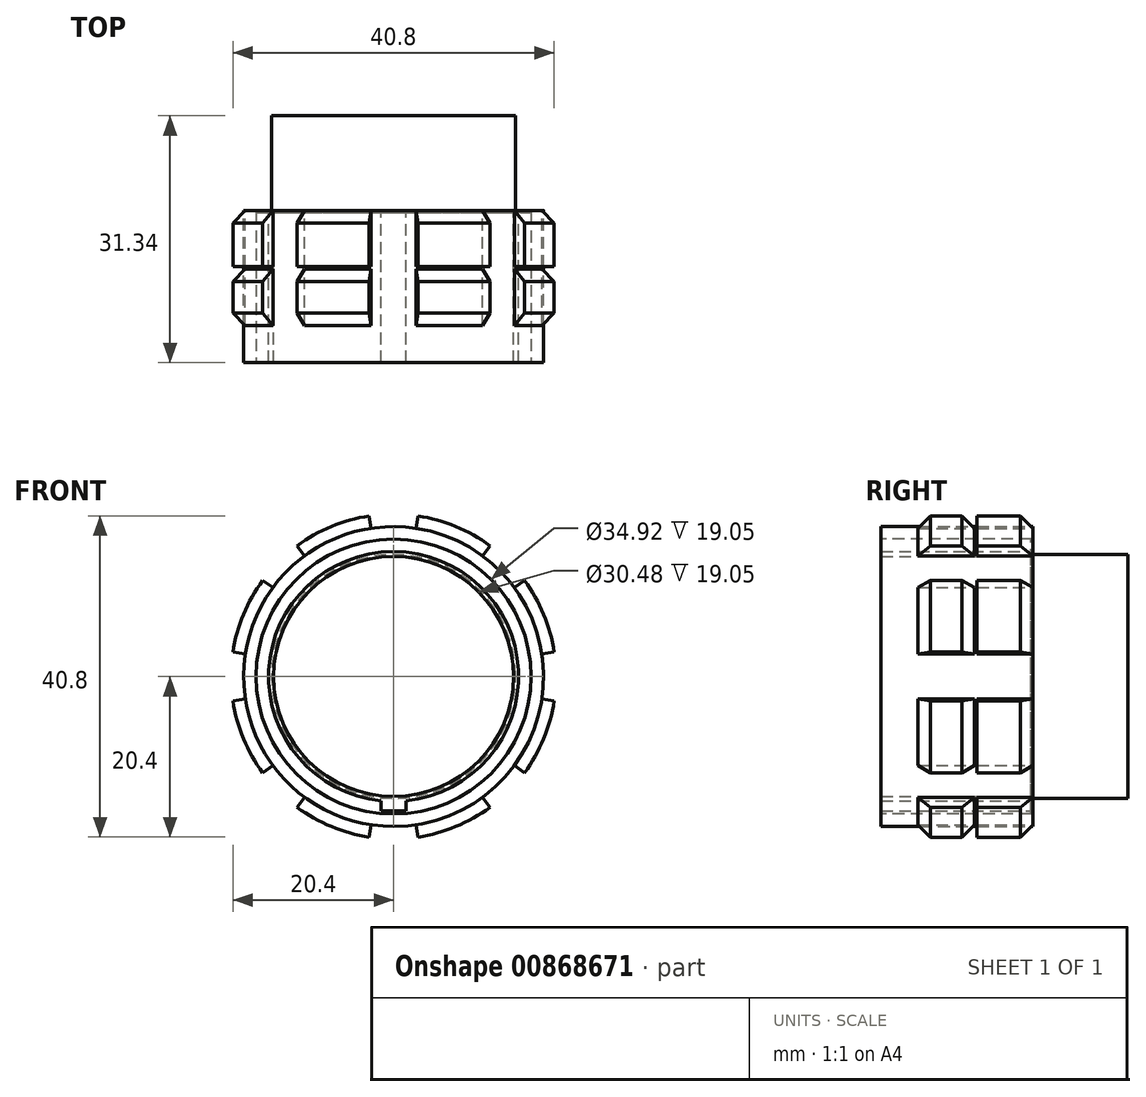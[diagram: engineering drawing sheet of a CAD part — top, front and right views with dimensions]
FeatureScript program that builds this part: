
annotation { "Feature Type Name" : "Feature", "Feature Type Description" : "" }
export const myFeature = defineFeature(function(context is Context, id is Id, definition is map)
    precondition{}
    {
        {
            var Q0;
            Q0=qCreatedBy(makeId("Front.planeOp"),FACE);
            var sketch = newSketch(context, id + "F0", { "sketchPlane" : qUnion([Q0])});
            skCircle(sketch, "E0", {"center": v(0, 0) * mm, "radius": 19.05 * mm});
            skSolve(sketch);
        }
        {
            var Q0;
            Q0 = qSketchRegion(id + "F0", true);
            extrude(context, id + "F1", {"entities" : qUnion([Q0]), "endBound" : BoundingType.SYMMETRIC, "depth" : 31.34 * mm, "offsetDistance" : 25.4 * mm});
        }
        {
            var Q0;
            Q0=makeQuery(id+"F1.opExtrude","CAP_FACE",FACE,{"disambiguationData":[OSD([sQuery(id+"F0.wireOp",EDGE,"E0")])],"isStart":false});
            cPlane(context, id + "F2", {"entities" : qUnion([Q0]), "cplaneType" : CPlaneType.OFFSET, "offset" : 4.7 * mm, "oppositeDirection" : true, "width" : 152.4 * mm, "height" : 152.4 * mm});
        }
        {
            var Q0;
            Q0=qCreatedBy(id+"F2.planeOp",FACE);
            var sketch = newSketch(context, id + "F3", { "sketchPlane" : qUnion([Q0])});
            skCircle(sketch, "E1", {"center": v(0, 0) * mm, "radius": 20.64 * mm});
            skLineSegment(sketch, "E2", {"start": v(0, 0) * mm, "end": v(-3.1, -20.4) * mm});
            skLineSegment(sketch, "E3", {"start": v(0, 0) * mm, "end": v(3.1, -20.4) * mm});
            skLineSegment(sketch, "E4", {"start": v(0, 0) * mm, "end": v(0, -20.64) * mm, "construction": true});
            skLineSegment(sketch, "E5.1.0", {"start": v(0, 0) * mm, "end": v(12.24, -16.62) * mm});
            skLineSegment(sketch, "E5.1.1", {"start": v(0, 0) * mm, "end": v(14.6, -14.6) * mm, "construction": true});
            skLineSegment(sketch, "E5.1.2", {"start": v(0, 0) * mm, "end": v(16.62, -12.24) * mm});
            skLineSegment(sketch, "E5.2.0", {"start": v(0, 0) * mm, "end": v(20.4, -3.1) * mm});
            skLineSegment(sketch, "E5.2.1", {"start": v(0, 0) * mm, "end": v(20.64, 0) * mm, "construction": true});
            skLineSegment(sketch, "E5.2.2", {"start": v(0, 0) * mm, "end": v(20.4, 3.1) * mm});
            skLineSegment(sketch, "E5.3.0", {"start": v(0, 0) * mm, "end": v(16.62, 12.24) * mm});
            skLineSegment(sketch, "E5.3.1", {"start": v(0, 0) * mm, "end": v(14.6, 14.6) * mm, "construction": true});
            skLineSegment(sketch, "E5.3.2", {"start": v(0, 0) * mm, "end": v(12.24, 16.62) * mm});
            skLineSegment(sketch, "E5.4.0", {"start": v(0, 0) * mm, "end": v(3.1, 20.4) * mm});
            skLineSegment(sketch, "E5.4.1", {"start": v(0, 0) * mm, "end": v(0, 20.64) * mm, "construction": true});
            skLineSegment(sketch, "E5.4.2", {"start": v(0, 0) * mm, "end": v(-3.1, 20.4) * mm});
            skLineSegment(sketch, "E5.5.0", {"start": v(0, 0) * mm, "end": v(-12.24, 16.62) * mm});
            skLineSegment(sketch, "E5.5.1", {"start": v(0, 0) * mm, "end": v(-14.6, 14.6) * mm, "construction": true});
            skLineSegment(sketch, "E5.5.2", {"start": v(0, 0) * mm, "end": v(-16.62, 12.24) * mm});
            skLineSegment(sketch, "E5.6.0", {"start": v(0, 0) * mm, "end": v(-20.4, 3.1) * mm});
            skLineSegment(sketch, "E5.6.1", {"start": v(0, 0) * mm, "end": v(-20.64, 0) * mm, "construction": true});
            skLineSegment(sketch, "E5.6.2", {"start": v(0, 0) * mm, "end": v(-20.4, -3.1) * mm});
            skLineSegment(sketch, "E5.7.0", {"start": v(0, 0) * mm, "end": v(-16.62, -12.24) * mm});
            skLineSegment(sketch, "E5.7.1", {"start": v(0, 0) * mm, "end": v(-14.6, -14.6) * mm, "construction": true});
            skLineSegment(sketch, "E5.7.2", {"start": v(0, 0) * mm, "end": v(-12.24, -16.62) * mm});
            skSolve(sketch);
        }
        {
            var Q0;
            {var subQ0=sQuery(id+"F3.wireOp",EDGE,"E5.5.2");Q0=makeQuery(id+"F3.imprint","IMPRINT",FACE,{"disambiguationData":[TD([[makeQuery(id+"F3.imprint","IMPRINT",EDGE,{"derivedFrom":subQ0}),1.0]])]});}
            var Q1;
            {var subQ0=sQuery(id+"F3.wireOp",EDGE,"E5.4.2");Q1=makeQuery(id+"F3.imprint","IMPRINT",FACE,{"disambiguationData":[TD([[makeQuery(id+"F3.imprint","IMPRINT",EDGE,{"derivedFrom":subQ0}),1.0]])]});}
            var Q2;
            {var subQ0=sQuery(id+"F3.wireOp",EDGE,"E5.3.2");Q2=makeQuery(id+"F3.imprint","IMPRINT",FACE,{"disambiguationData":[TD([[makeQuery(id+"F3.imprint","IMPRINT",EDGE,{"derivedFrom":subQ0}),1.0]])]});}
            var Q3;
            {var subQ0=sQuery(id+"F3.wireOp",EDGE,"E5.2.2");Q3=makeQuery(id+"F3.imprint","IMPRINT",FACE,{"disambiguationData":[TD([[makeQuery(id+"F3.imprint","IMPRINT",EDGE,{"derivedFrom":subQ0}),1.0]])]});}
            var Q4;
            {var subQ0=sQuery(id+"F3.wireOp",EDGE,"E5.1.2");Q4=makeQuery(id+"F3.imprint","IMPRINT",FACE,{"disambiguationData":[TD([[makeQuery(id+"F3.imprint","IMPRINT",EDGE,{"derivedFrom":subQ0}),1.0]])]});}
            var Q5;
            {var subQ0=sQuery(id+"F3.wireOp",EDGE,"E3");Q5=makeQuery(id+"F3.imprint","IMPRINT",FACE,{"disambiguationData":[TD([[makeQuery(id+"F3.imprint","IMPRINT",EDGE,{"derivedFrom":subQ0}),1.0]])]});}
            var Q6;
            {var subQ0=sQuery(id+"F3.wireOp",EDGE,"E2");Q6=makeQuery(id+"F3.imprint","IMPRINT",FACE,{"disambiguationData":[TD([[makeQuery(id+"F3.imprint","IMPRINT",EDGE,{"derivedFrom":subQ0}),-1.0]])]});}
            var Q7;
            {var subQ0=sQuery(id+"F3.wireOp",EDGE,"E5.6.2");Q7=makeQuery(id+"F3.imprint","IMPRINT",FACE,{"disambiguationData":[TD([[makeQuery(id+"F3.imprint","IMPRINT",EDGE,{"derivedFrom":subQ0}),1.0]])]});}
            extrude(context, id + "F4", {"entities" : qUnion([Q0, Q1, Q2, Q3, Q4, Q5, Q6, Q7]), "operationType" : NewBodyOperationType.ADD, "oppositeDirection" : true, "depth" : 14.6 * mm, "offsetDistance" : 25.4 * mm});
        }
        {
            var Q0;
            Q0=makeQuery(id+"F1.opExtrude","CAP_FACE",FACE,{"disambiguationData":[OSD([sQuery(id+"F0.wireOp",EDGE,"E0")])],"isStart":false});
            var sketch = newSketch(context, id + "F5", { "sketchPlane" : qUnion([Q0])});
            skCircle(sketch, "E6", {"center": v(0, 0) * mm, "radius": 17.46 * mm});
            skSolve(sketch);
        }
        {
            var Q0;
            Q0 = qSketchRegion(id + "F5", true);
            extrude(context, id + "F6", {"entities" : qUnion([Q0]), "operationType" : NewBodyOperationType.REMOVE, "oppositeDirection" : true, "depth" : 19.05 * mm, "offsetDistance" : 25.4 * mm});
        }
        {
            var Q0;
            Q0=makeQuery(id+"F1.opExtrude","CAP_FACE",FACE,{"disambiguationData":[OSD([sQuery(id+"F0.wireOp",EDGE,"E0")])],"isStart":true});
            var sketch = newSketch(context, id + "F7", { "sketchPlane" : qUnion([Q0])});
            skCircle(sketch, "E7", {"center": v(0, 0) * mm, "radius": 15.5 * mm});
            skSolve(sketch);
        }
        {
            var Q0;
            Q0=makeQuery(id+"F7.imprint","IMPRINT",FACE,{"disambiguationData":[TD([[makeQuery(id+"F7.imprint","IMPRINT",EDGE,{"derivedFrom":sQuery(id+"F7.wireOp",EDGE,"E7")}),-1.0]])]});
            extrude(context, id + "F8", {"entities" : qUnion([Q0]), "operationType" : NewBodyOperationType.REMOVE, "oppositeDirection" : true, "depth" : 12.04 * mm, "offsetDistance" : 25.4 * mm});
        }
        {
            var Q0;
            Q0=qCreatedBy(id+"F2.planeOp",FACE);
            cPlane(context, id + "F9", {"entities" : qUnion([Q0]), "cplaneType" : CPlaneType.OFFSET, "offset" : 7.3 * mm, "oppositeDirection" : true, "width" : 152.4 * mm, "height" : 152.4 * mm});
        }
        {
            var Q0;
            Q0=qCreatedBy(id+"F9.planeOp",FACE);
            var sketch = newSketch(context, id + "F10", { "sketchPlane" : qUnion([Q0])});
            skCircle(sketch, "E8", {"center": v(0, 0) * mm, "radius": 20.64 * mm});
            skCircle(sketch, "E9", {"center": v(0, 0) * mm, "radius": 19.05 * mm});
            skSolve(sketch);
        }
        {
            var Q0;
            Q0 = qSketchRegion(id + "F10", true);
            extrude(context, id + "F11", {"entities" : qUnion([Q0]), "operationType" : NewBodyOperationType.REMOVE, "endBound" : BoundingType.SYMMETRIC, "oppositeDirection" : true, "depth" : 0.32 * mm, "offsetDistance" : 25.4 * mm});
        }
        {
            var Q0;
            {var subQ0=sQuery(id+"F3.wireOp",EDGE,"E1");var subQ1=sQuery(id+"F10.wireOp",EDGE,"E8");Q0=makeQuery(id+"F11.boolean.opBoolean","COPY",EDGE,{"disambiguationData":[topologyDisambiguationEdgeConnected([makeQuery(id+"F4.opExtrude","SWEPT_FACE",FACE,{"disambiguationData":[OSD([subQ0]),TDD([makeQuery(id+"F3.imprint","IMPRINT",EDGE,{"disambiguationData":[TD([[makeQuery(id+"F3.imprint","INTERSECT",VERTEX,{"derivedFrom":[subQ0,sQuery(id+"F3.wireOp",EDGE,"E5.4.2")]}),-1.0]])],"derivedFrom":subQ0})])]})])],"derivedFrom":makeQuery(id+"F11.opExtrude","CAP_EDGE",EDGE,{"disambiguationData":[OSD([subQ1])],"isStart":false})});}
            var Q1;
            {var subQ0=sQuery(id+"F3.wireOp",EDGE,"E1");var subQ1=sQuery(id+"F10.wireOp",EDGE,"E8");Q1=makeQuery(id+"F11.boolean.opBoolean","COPY",EDGE,{"disambiguationData":[topologyDisambiguationEdgeConnected([makeQuery(id+"F4.opExtrude","SWEPT_FACE",FACE,{"disambiguationData":[OSD([subQ0]),TDD([makeQuery(id+"F3.imprint","IMPRINT",EDGE,{"disambiguationData":[TD([[makeQuery(id+"F3.imprint","INTERSECT",VERTEX,{"derivedFrom":[subQ0,sQuery(id+"F3.wireOp",EDGE,"E5.4.2")]}),-1.0]])],"derivedFrom":subQ0})])]})])],"derivedFrom":makeQuery(id+"F11.opExtrude","CAP_EDGE",EDGE,{"disambiguationData":[OSD([subQ1])],"isStart":true})});}
            var Q2;
            {var subQ0=sQuery(id+"F3.wireOp",EDGE,"E1");Q2=makeQuery(id+"F4.opExtrude","CAP_EDGE",EDGE,{"disambiguationData":[OSD([subQ0]),TDD([makeQuery(id+"F3.imprint","IMPRINT",EDGE,{"disambiguationData":[TD([[makeQuery(id+"F3.imprint","INTERSECT",VERTEX,{"derivedFrom":[subQ0,sQuery(id+"F3.wireOp",EDGE,"E5.4.2")]}),-1.0]])],"derivedFrom":subQ0})])],"isStart":true});}
            var Q3;
            {var subQ0=sQuery(id+"F3.wireOp",EDGE,"E1");Q3=makeQuery(id+"F4.opExtrude","CAP_EDGE",EDGE,{"disambiguationData":[OSD([subQ0]),TDD([makeQuery(id+"F3.imprint","IMPRINT",EDGE,{"disambiguationData":[TD([[makeQuery(id+"F3.imprint","INTERSECT",VERTEX,{"derivedFrom":[subQ0,sQuery(id+"F3.wireOp",EDGE,"E5.4.2")]}),-1.0]])],"derivedFrom":subQ0})])],"isStart":false});}
            var Q4;
            {var subQ0=sQuery(id+"F3.wireOp",EDGE,"E1");Q4=makeQuery(id+"F4.opExtrude","CAP_EDGE",EDGE,{"disambiguationData":[OSD([subQ0]),TDD([makeQuery(id+"F3.imprint","IMPRINT",EDGE,{"disambiguationData":[TD([[makeQuery(id+"F3.imprint","INTERSECT",VERTEX,{"derivedFrom":[subQ0,sQuery(id+"F3.wireOp",EDGE,"E5.5.2")]}),-1.0]])],"derivedFrom":subQ0})])],"isStart":false});}
            var Q5;
            {var subQ0=sQuery(id+"F3.wireOp",EDGE,"E1");var subQ1=sQuery(id+"F10.wireOp",EDGE,"E8");Q5=makeQuery(id+"F11.boolean.opBoolean","COPY",EDGE,{"disambiguationData":[topologyDisambiguationEdgeConnected([makeQuery(id+"F4.opExtrude","SWEPT_FACE",FACE,{"disambiguationData":[OSD([subQ0]),TDD([makeQuery(id+"F3.imprint","IMPRINT",EDGE,{"disambiguationData":[TD([[makeQuery(id+"F3.imprint","INTERSECT",VERTEX,{"derivedFrom":[subQ0,sQuery(id+"F3.wireOp",EDGE,"E5.5.2")]}),-1.0]])],"derivedFrom":subQ0})])]})])],"derivedFrom":makeQuery(id+"F11.opExtrude","CAP_EDGE",EDGE,{"disambiguationData":[OSD([subQ1])],"isStart":false})});}
            var Q6;
            {var subQ0=sQuery(id+"F3.wireOp",EDGE,"E1");var subQ1=sQuery(id+"F10.wireOp",EDGE,"E8");Q6=makeQuery(id+"F11.boolean.opBoolean","COPY",EDGE,{"disambiguationData":[topologyDisambiguationEdgeConnected([makeQuery(id+"F4.opExtrude","SWEPT_FACE",FACE,{"disambiguationData":[OSD([subQ0]),TDD([makeQuery(id+"F3.imprint","IMPRINT",EDGE,{"disambiguationData":[TD([[makeQuery(id+"F3.imprint","INTERSECT",VERTEX,{"derivedFrom":[subQ0,sQuery(id+"F3.wireOp",EDGE,"E5.5.2")]}),-1.0]])],"derivedFrom":subQ0})])]})])],"derivedFrom":makeQuery(id+"F11.opExtrude","CAP_EDGE",EDGE,{"disambiguationData":[OSD([subQ1])],"isStart":true})});}
            var Q7;
            {var subQ0=sQuery(id+"F3.wireOp",EDGE,"E1");Q7=makeQuery(id+"F4.opExtrude","CAP_EDGE",EDGE,{"disambiguationData":[OSD([subQ0]),TDD([makeQuery(id+"F3.imprint","IMPRINT",EDGE,{"disambiguationData":[TD([[makeQuery(id+"F3.imprint","INTERSECT",VERTEX,{"derivedFrom":[subQ0,sQuery(id+"F3.wireOp",EDGE,"E5.5.2")]}),-1.0]])],"derivedFrom":subQ0})])],"isStart":true});}
            var Q8;
            {var subQ0=sQuery(id+"F3.wireOp",EDGE,"E1");Q8=makeQuery(id+"F4.opExtrude","CAP_EDGE",EDGE,{"disambiguationData":[OSD([subQ0]),TDD([makeQuery(id+"F3.imprint","IMPRINT",EDGE,{"disambiguationData":[TD([[makeQuery(id+"F3.imprint","INTERSECT",VERTEX,{"derivedFrom":[subQ0,sQuery(id+"F3.wireOp",EDGE,"E5.6.2")]}),-1.0]])],"derivedFrom":subQ0})])],"isStart":true});}
            var Q9;
            {var subQ0=sQuery(id+"F3.wireOp",EDGE,"E1");var subQ1=sQuery(id+"F10.wireOp",EDGE,"E8");Q9=makeQuery(id+"F11.boolean.opBoolean","COPY",EDGE,{"disambiguationData":[topologyDisambiguationEdgeConnected([makeQuery(id+"F4.opExtrude","SWEPT_FACE",FACE,{"disambiguationData":[OSD([subQ0]),TDD([makeQuery(id+"F3.imprint","IMPRINT",EDGE,{"disambiguationData":[TD([[makeQuery(id+"F3.imprint","INTERSECT",VERTEX,{"derivedFrom":[subQ0,sQuery(id+"F3.wireOp",EDGE,"E5.6.2")]}),-1.0]])],"derivedFrom":subQ0})])]})])],"derivedFrom":makeQuery(id+"F11.opExtrude","CAP_EDGE",EDGE,{"disambiguationData":[OSD([subQ1])],"isStart":true})});}
            var Q10;
            {var subQ0=sQuery(id+"F3.wireOp",EDGE,"E1");var subQ1=sQuery(id+"F10.wireOp",EDGE,"E8");Q10=makeQuery(id+"F11.boolean.opBoolean","COPY",EDGE,{"disambiguationData":[topologyDisambiguationEdgeConnected([makeQuery(id+"F4.opExtrude","SWEPT_FACE",FACE,{"disambiguationData":[OSD([subQ0]),TDD([makeQuery(id+"F3.imprint","IMPRINT",EDGE,{"disambiguationData":[TD([[makeQuery(id+"F3.imprint","INTERSECT",VERTEX,{"derivedFrom":[subQ0,sQuery(id+"F3.wireOp",EDGE,"E5.6.2")]}),-1.0]])],"derivedFrom":subQ0})])]})])],"derivedFrom":makeQuery(id+"F11.opExtrude","CAP_EDGE",EDGE,{"disambiguationData":[OSD([subQ1])],"isStart":false})});}
            var Q11;
            {var subQ0=sQuery(id+"F3.wireOp",EDGE,"E1");Q11=makeQuery(id+"F4.opExtrude","CAP_EDGE",EDGE,{"disambiguationData":[OSD([subQ0]),TDD([makeQuery(id+"F3.imprint","IMPRINT",EDGE,{"disambiguationData":[TD([[makeQuery(id+"F3.imprint","INTERSECT",VERTEX,{"derivedFrom":[subQ0,sQuery(id+"F3.wireOp",EDGE,"E5.6.2")]}),-1.0]])],"derivedFrom":subQ0})])],"isStart":false});}
            var Q12;
            {var subQ0=sQuery(id+"F3.wireOp",EDGE,"E1");Q12=makeQuery(id+"F4.opExtrude","CAP_EDGE",EDGE,{"disambiguationData":[OSD([subQ0]),TDD([makeQuery(id+"F3.imprint","IMPRINT",EDGE,{"disambiguationData":[TD([[makeQuery(id+"F3.imprint","INTERSECT",VERTEX,{"derivedFrom":[subQ0,sQuery(id+"F3.wireOp",EDGE,"E2")]}),1.0]])],"derivedFrom":subQ0})])],"isStart":true});}
            var Q13;
            {var subQ0=sQuery(id+"F3.wireOp",EDGE,"E1");var subQ1=sQuery(id+"F10.wireOp",EDGE,"E8");Q13=makeQuery(id+"F11.boolean.opBoolean","COPY",EDGE,{"disambiguationData":[topologyDisambiguationEdgeConnected([makeQuery(id+"F4.opExtrude","SWEPT_FACE",FACE,{"disambiguationData":[OSD([subQ0]),TDD([makeQuery(id+"F3.imprint","IMPRINT",EDGE,{"disambiguationData":[TD([[makeQuery(id+"F3.imprint","INTERSECT",VERTEX,{"derivedFrom":[subQ0,sQuery(id+"F3.wireOp",EDGE,"E2")]}),1.0]])],"derivedFrom":subQ0})])]})])],"derivedFrom":makeQuery(id+"F11.opExtrude","CAP_EDGE",EDGE,{"disambiguationData":[OSD([subQ1])],"isStart":true})});}
            var Q14;
            {var subQ0=sQuery(id+"F3.wireOp",EDGE,"E1");var subQ1=sQuery(id+"F10.wireOp",EDGE,"E8");Q14=makeQuery(id+"F11.boolean.opBoolean","COPY",EDGE,{"disambiguationData":[topologyDisambiguationEdgeConnected([makeQuery(id+"F4.opExtrude","SWEPT_FACE",FACE,{"disambiguationData":[OSD([subQ0]),TDD([makeQuery(id+"F3.imprint","IMPRINT",EDGE,{"disambiguationData":[TD([[makeQuery(id+"F3.imprint","INTERSECT",VERTEX,{"derivedFrom":[subQ0,sQuery(id+"F3.wireOp",EDGE,"E2")]}),1.0]])],"derivedFrom":subQ0})])]})])],"derivedFrom":makeQuery(id+"F11.opExtrude","CAP_EDGE",EDGE,{"disambiguationData":[OSD([subQ1])],"isStart":false})});}
            var Q15;
            {var subQ0=sQuery(id+"F3.wireOp",EDGE,"E1");Q15=makeQuery(id+"F4.opExtrude","CAP_EDGE",EDGE,{"disambiguationData":[OSD([subQ0]),TDD([makeQuery(id+"F3.imprint","IMPRINT",EDGE,{"disambiguationData":[TD([[makeQuery(id+"F3.imprint","INTERSECT",VERTEX,{"derivedFrom":[subQ0,sQuery(id+"F3.wireOp",EDGE,"E2")]}),1.0]])],"derivedFrom":subQ0})])],"isStart":false});}
            var Q16;
            {var subQ0=sQuery(id+"F3.wireOp",EDGE,"E1");var subQ1=sQuery(id+"F10.wireOp",EDGE,"E8");Q16=makeQuery(id+"F11.boolean.opBoolean","COPY",EDGE,{"disambiguationData":[topologyDisambiguationEdgeConnected([makeQuery(id+"F4.opExtrude","SWEPT_FACE",FACE,{"disambiguationData":[OSD([subQ0]),TDD([makeQuery(id+"F3.imprint","IMPRINT",EDGE,{"disambiguationData":[TD([[makeQuery(id+"F3.imprint","INTERSECT",VERTEX,{"derivedFrom":[subQ0,sQuery(id+"F3.wireOp",EDGE,"E3")]}),-1.0]])],"derivedFrom":subQ0})])]})])],"derivedFrom":makeQuery(id+"F11.opExtrude","CAP_EDGE",EDGE,{"disambiguationData":[OSD([subQ1])],"isStart":true})});}
            var Q17;
            {var subQ0=sQuery(id+"F3.wireOp",EDGE,"E1");Q17=makeQuery(id+"F4.opExtrude","CAP_EDGE",EDGE,{"disambiguationData":[OSD([subQ0]),TDD([makeQuery(id+"F3.imprint","IMPRINT",EDGE,{"disambiguationData":[TD([[makeQuery(id+"F3.imprint","INTERSECT",VERTEX,{"derivedFrom":[subQ0,sQuery(id+"F3.wireOp",EDGE,"E3")]}),-1.0]])],"derivedFrom":subQ0})])],"isStart":true});}
            var Q18;
            {var subQ0=sQuery(id+"F3.wireOp",EDGE,"E1");var subQ1=sQuery(id+"F10.wireOp",EDGE,"E8");Q18=makeQuery(id+"F11.boolean.opBoolean","COPY",EDGE,{"disambiguationData":[topologyDisambiguationEdgeConnected([makeQuery(id+"F4.opExtrude","SWEPT_FACE",FACE,{"disambiguationData":[OSD([subQ0]),TDD([makeQuery(id+"F3.imprint","IMPRINT",EDGE,{"disambiguationData":[TD([[makeQuery(id+"F3.imprint","INTERSECT",VERTEX,{"derivedFrom":[subQ0,sQuery(id+"F3.wireOp",EDGE,"E3")]}),-1.0]])],"derivedFrom":subQ0})])]})])],"derivedFrom":makeQuery(id+"F11.opExtrude","CAP_EDGE",EDGE,{"disambiguationData":[OSD([subQ1])],"isStart":false})});}
            var Q19;
            {var subQ0=sQuery(id+"F3.wireOp",EDGE,"E1");Q19=makeQuery(id+"F4.opExtrude","CAP_EDGE",EDGE,{"disambiguationData":[OSD([subQ0]),TDD([makeQuery(id+"F3.imprint","IMPRINT",EDGE,{"disambiguationData":[TD([[makeQuery(id+"F3.imprint","INTERSECT",VERTEX,{"derivedFrom":[subQ0,sQuery(id+"F3.wireOp",EDGE,"E3")]}),-1.0]])],"derivedFrom":subQ0})])],"isStart":false});}
            var Q20;
            {var subQ0=sQuery(id+"F3.wireOp",EDGE,"E1");Q20=makeQuery(id+"F4.opExtrude","CAP_EDGE",EDGE,{"disambiguationData":[OSD([subQ0]),TDD([makeQuery(id+"F3.imprint","IMPRINT",EDGE,{"disambiguationData":[TD([[makeQuery(id+"F3.imprint","INTERSECT",VERTEX,{"derivedFrom":[subQ0,sQuery(id+"F3.wireOp",EDGE,"E5.1.2")]}),-1.0]])],"derivedFrom":subQ0})])],"isStart":false});}
            var Q21;
            {var subQ0=sQuery(id+"F3.wireOp",EDGE,"E1");var subQ1=sQuery(id+"F10.wireOp",EDGE,"E8");Q21=makeQuery(id+"F11.boolean.opBoolean","COPY",EDGE,{"disambiguationData":[topologyDisambiguationEdgeConnected([makeQuery(id+"F4.opExtrude","SWEPT_FACE",FACE,{"disambiguationData":[OSD([subQ0]),TDD([makeQuery(id+"F3.imprint","IMPRINT",EDGE,{"disambiguationData":[TD([[makeQuery(id+"F3.imprint","INTERSECT",VERTEX,{"derivedFrom":[subQ0,sQuery(id+"F3.wireOp",EDGE,"E5.1.2")]}),-1.0]])],"derivedFrom":subQ0})])]})])],"derivedFrom":makeQuery(id+"F11.opExtrude","CAP_EDGE",EDGE,{"disambiguationData":[OSD([subQ1])],"isStart":false})});}
            var Q22;
            {var subQ0=sQuery(id+"F3.wireOp",EDGE,"E1");var subQ1=sQuery(id+"F10.wireOp",EDGE,"E8");Q22=makeQuery(id+"F11.boolean.opBoolean","COPY",EDGE,{"disambiguationData":[topologyDisambiguationEdgeConnected([makeQuery(id+"F4.opExtrude","SWEPT_FACE",FACE,{"disambiguationData":[OSD([subQ0]),TDD([makeQuery(id+"F3.imprint","IMPRINT",EDGE,{"disambiguationData":[TD([[makeQuery(id+"F3.imprint","INTERSECT",VERTEX,{"derivedFrom":[subQ0,sQuery(id+"F3.wireOp",EDGE,"E5.1.2")]}),-1.0]])],"derivedFrom":subQ0})])]})])],"derivedFrom":makeQuery(id+"F11.opExtrude","CAP_EDGE",EDGE,{"disambiguationData":[OSD([subQ1])],"isStart":true})});}
            var Q23;
            {var subQ0=sQuery(id+"F3.wireOp",EDGE,"E1");Q23=makeQuery(id+"F4.opExtrude","CAP_EDGE",EDGE,{"disambiguationData":[OSD([subQ0]),TDD([makeQuery(id+"F3.imprint","IMPRINT",EDGE,{"disambiguationData":[TD([[makeQuery(id+"F3.imprint","INTERSECT",VERTEX,{"derivedFrom":[subQ0,sQuery(id+"F3.wireOp",EDGE,"E5.1.2")]}),-1.0]])],"derivedFrom":subQ0})])],"isStart":true});}
            var Q24;
            {var subQ0=sQuery(id+"F3.wireOp",EDGE,"E1");Q24=makeQuery(id+"F4.opExtrude","CAP_EDGE",EDGE,{"disambiguationData":[OSD([subQ0]),TDD([makeQuery(id+"F3.imprint","IMPRINT",EDGE,{"disambiguationData":[TD([[makeQuery(id+"F3.imprint","INTERSECT",VERTEX,{"derivedFrom":[subQ0,sQuery(id+"F3.wireOp",EDGE,"E5.2.2")]}),-1.0]])],"derivedFrom":subQ0})])],"isStart":false});}
            var Q25;
            {var subQ0=sQuery(id+"F3.wireOp",EDGE,"E1");var subQ1=sQuery(id+"F10.wireOp",EDGE,"E8");Q25=makeQuery(id+"F11.boolean.opBoolean","COPY",EDGE,{"disambiguationData":[topologyDisambiguationEdgeConnected([makeQuery(id+"F4.opExtrude","SWEPT_FACE",FACE,{"disambiguationData":[OSD([subQ0]),TDD([makeQuery(id+"F3.imprint","IMPRINT",EDGE,{"disambiguationData":[TD([[makeQuery(id+"F3.imprint","INTERSECT",VERTEX,{"derivedFrom":[subQ0,sQuery(id+"F3.wireOp",EDGE,"E5.2.2")]}),-1.0]])],"derivedFrom":subQ0})])]})])],"derivedFrom":makeQuery(id+"F11.opExtrude","CAP_EDGE",EDGE,{"disambiguationData":[OSD([subQ1])],"isStart":false})});}
            var Q26;
            {var subQ0=sQuery(id+"F3.wireOp",EDGE,"E1");var subQ1=sQuery(id+"F10.wireOp",EDGE,"E8");Q26=makeQuery(id+"F11.boolean.opBoolean","COPY",EDGE,{"disambiguationData":[topologyDisambiguationEdgeConnected([makeQuery(id+"F4.opExtrude","SWEPT_FACE",FACE,{"disambiguationData":[OSD([subQ0]),TDD([makeQuery(id+"F3.imprint","IMPRINT",EDGE,{"disambiguationData":[TD([[makeQuery(id+"F3.imprint","INTERSECT",VERTEX,{"derivedFrom":[subQ0,sQuery(id+"F3.wireOp",EDGE,"E5.2.2")]}),-1.0]])],"derivedFrom":subQ0})])]})])],"derivedFrom":makeQuery(id+"F11.opExtrude","CAP_EDGE",EDGE,{"disambiguationData":[OSD([subQ1])],"isStart":true})});}
            var Q27;
            {var subQ0=sQuery(id+"F3.wireOp",EDGE,"E1");Q27=makeQuery(id+"F4.opExtrude","CAP_EDGE",EDGE,{"disambiguationData":[OSD([subQ0]),TDD([makeQuery(id+"F3.imprint","IMPRINT",EDGE,{"disambiguationData":[TD([[makeQuery(id+"F3.imprint","INTERSECT",VERTEX,{"derivedFrom":[subQ0,sQuery(id+"F3.wireOp",EDGE,"E5.2.2")]}),-1.0]])],"derivedFrom":subQ0})])],"isStart":true});}
            var Q28;
            {var subQ0=sQuery(id+"F3.wireOp",EDGE,"E1");Q28=makeQuery(id+"F4.opExtrude","CAP_EDGE",EDGE,{"disambiguationData":[OSD([subQ0]),TDD([makeQuery(id+"F3.imprint","IMPRINT",EDGE,{"disambiguationData":[TD([[makeQuery(id+"F3.imprint","INTERSECT",VERTEX,{"derivedFrom":[subQ0,sQuery(id+"F3.wireOp",EDGE,"E5.3.2")]}),-1.0]])],"derivedFrom":subQ0})])],"isStart":false});}
            var Q29;
            {var subQ0=sQuery(id+"F3.wireOp",EDGE,"E1");var subQ1=sQuery(id+"F10.wireOp",EDGE,"E8");Q29=makeQuery(id+"F11.boolean.opBoolean","COPY",EDGE,{"disambiguationData":[topologyDisambiguationEdgeConnected([makeQuery(id+"F4.opExtrude","SWEPT_FACE",FACE,{"disambiguationData":[OSD([subQ0]),TDD([makeQuery(id+"F3.imprint","IMPRINT",EDGE,{"disambiguationData":[TD([[makeQuery(id+"F3.imprint","INTERSECT",VERTEX,{"derivedFrom":[subQ0,sQuery(id+"F3.wireOp",EDGE,"E5.3.2")]}),-1.0]])],"derivedFrom":subQ0})])]})])],"derivedFrom":makeQuery(id+"F11.opExtrude","CAP_EDGE",EDGE,{"disambiguationData":[OSD([subQ1])],"isStart":false})});}
            var Q30;
            {var subQ0=sQuery(id+"F3.wireOp",EDGE,"E1");var subQ1=sQuery(id+"F10.wireOp",EDGE,"E8");Q30=makeQuery(id+"F11.boolean.opBoolean","COPY",EDGE,{"disambiguationData":[topologyDisambiguationEdgeConnected([makeQuery(id+"F4.opExtrude","SWEPT_FACE",FACE,{"disambiguationData":[OSD([subQ0]),TDD([makeQuery(id+"F3.imprint","IMPRINT",EDGE,{"disambiguationData":[TD([[makeQuery(id+"F3.imprint","INTERSECT",VERTEX,{"derivedFrom":[subQ0,sQuery(id+"F3.wireOp",EDGE,"E5.3.2")]}),-1.0]])],"derivedFrom":subQ0})])]})])],"derivedFrom":makeQuery(id+"F11.opExtrude","CAP_EDGE",EDGE,{"disambiguationData":[OSD([subQ1])],"isStart":true})});}
            var Q31;
            {var subQ0=sQuery(id+"F3.wireOp",EDGE,"E1");Q31=makeQuery(id+"F4.opExtrude","CAP_EDGE",EDGE,{"disambiguationData":[OSD([subQ0]),TDD([makeQuery(id+"F3.imprint","IMPRINT",EDGE,{"disambiguationData":[TD([[makeQuery(id+"F3.imprint","INTERSECT",VERTEX,{"derivedFrom":[subQ0,sQuery(id+"F3.wireOp",EDGE,"E5.3.2")]}),-1.0]])],"derivedFrom":subQ0})])],"isStart":true});}
            chamfer(context, id + "F12", {"entities" : qUnion([Q0, Q1, Q2, Q3, Q4, Q5, Q6, Q7, Q8, Q9, Q10, Q11, Q12, Q13, Q14, Q15, Q16, Q17, Q18, Q19, Q20, Q21, Q22, Q23, Q24, Q25, Q26, Q27, Q28, Q29, Q30, Q31]), "width" : 1.59 * mm, "tangentPropagation" : true});
        }
        {
            var Q0;
            Q0=makeQuery(id+"F6.boolean.opBoolean","COPY",FACE,{"derivedFrom":makeQuery(id+"F6.opExtrude","CAP_FACE",FACE,{"disambiguationData":[OSD([sQuery(id+"F5.wireOp",EDGE,"E6")])],"isStart":false})});
            var sketch = newSketch(context, id + "F13", { "sketchPlane" : qUnion([Q0])});
            skCircle(sketch, "E10", {"center": v(0, 0) * mm, "radius": 15.88 * mm});
            skCircle(sketch, "E11", {"center": v(0, 0) * mm, "radius": 15.24 * mm});
            skLineSegment(sketch, "E12.bottom", {"start": v(-1.59, -15.8) * mm, "end": v(1.59, -15.8) * mm});
            skLineSegment(sketch, "E12.top", {"start": v(-1.59, -17.07) * mm, "end": v(1.59, -17.07) * mm});
            skLineSegment(sketch, "E12.left", {"start": v(-1.59, -15.8) * mm, "end": v(-1.59, -17.07) * mm});
            skLineSegment(sketch, "E12.right", {"start": v(1.59, -15.8) * mm, "end": v(1.59, -17.07) * mm});
            skSolve(sketch);
        }
        {
            var Q0;
            Q0=makeQuery(id+"F13.imprint","IMPRINT",FACE,{"disambiguationData":[TD([[makeQuery(id+"F13.imprint","IMPRINT",EDGE,{"derivedFrom":sQuery(id+"F13.wireOp",EDGE,"E10")}),1.0]])]});
            var Q1;
            Q1=makeQuery(id+"F13.imprint","IMPRINT",FACE,{"disambiguationData":[TD([[makeQuery(id+"F13.imprint","IMPRINT",EDGE,{"derivedFrom":sQuery(id+"F13.wireOp",EDGE,"E12.top")}),1.0]])]});
            var Q2;
            Q2=makeQuery(id+"F13.imprint","IMPRINT",FACE,{"disambiguationData":[TD([[makeQuery(id+"F13.imprint","IMPRINT",EDGE,{"derivedFrom":sQuery(id+"F13.wireOp",EDGE,"E11")}),-1.0]])]});
            extrude(context, id + "F14", {"entities" : qUnion([Q0, Q1, Q2]), "operationType" : NewBodyOperationType.ADD, "depth" : 19.05 * mm, "offsetDistance" : 25.4 * mm});
        }
    });
